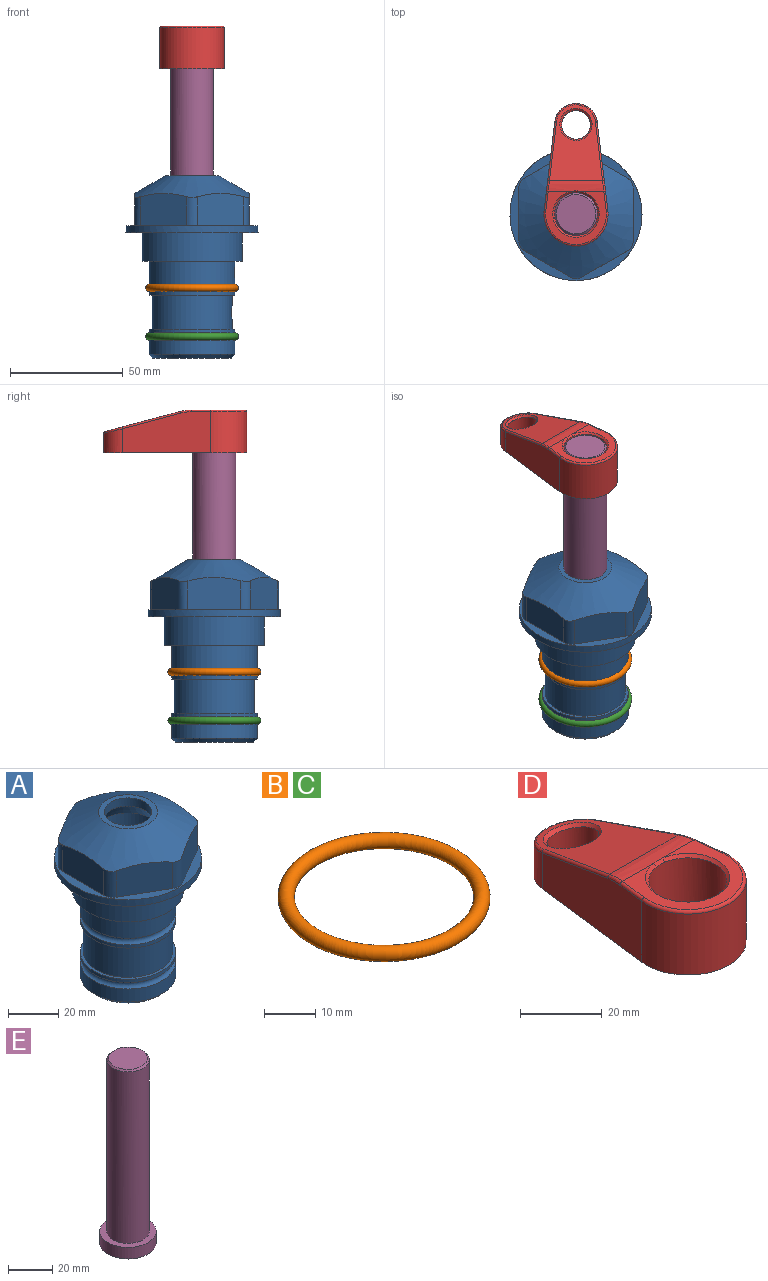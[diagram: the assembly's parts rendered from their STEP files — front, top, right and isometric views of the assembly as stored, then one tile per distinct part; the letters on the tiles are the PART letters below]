
ASSEMBLY  parts=5 mates=4
PART A: 36 faces, bbox 58.7x58.7x81 mm
  f0: cylinder r=17.78mm len=35.56mm, axis (0,0,1), area 1670.8mm2, adj f23,f24,f31
  f1: cylinder r=19.05mm len=38.1mm, axis (0,0,1), area 1191.9mm2, adj f26,f27,f30
  f2: plane 58.66x58.66mm, normal (0,0,-1), area 1150.6mm2, adj f3,f28
  f3: cylinder r=29.33mm len=58.66mm, axis (0,0,-1), area 585.1mm2, adj f2,f4
  f4: plane 58.66x58.66mm, normal (0,0,1), area 475.9mm2, adj f3,f5,f6,f7,f8,f9,f10,f11
  f5: plane 20.32x14.34mm, normal (-0.5,0.87,0), area 324.4mm2, adj f4,f15,f16,f17
  f6: plane 20.32x14.34mm, normal (0.5,0.87,0), area 324.4mm2, adj f4,f14,f15,f17
  f7: plane 23.48x14.34mm, normal (1,0,0), area 324.4mm2, adj f4,f13,f14,f17
  f8: plane 20.32x14.34mm, normal (0.5,-0.87,0), area 324.4mm2, adj f4,f12,f13,f17
  f9: plane 20.32x14.34mm, normal (-0.5,-0.87,0), area 324.4mm2, adj f4,f11,f12,f17
  f10: plane 23.48x14.34mm, normal (-1,0,0), area 324.4mm2, adj f4,f11,f16,f17
  f11: cylinder r=5.08mm len=12.85mm, axis (0,0,-1), area 67.2mm2, adj f4,f9,f10,f17
  f12: cylinder r=5.08mm len=12.85mm, axis (0,0,-1), area 67.2mm2, adj f4,f8,f9,f17
  f13: cylinder r=5.08mm len=12.85mm, axis (0,0,-1), area 67.2mm2, adj f4,f7,f8,f17
  f14: cylinder r=5.08mm len=12.85mm, axis (0,0,-1), area 67.2mm2, adj f4,f6,f7,f17
  f15: cylinder r=5.08mm len=12.85mm, axis (0,0,-1), area 67.2mm2, adj f4,f5,f6,f17
  f16: cylinder r=5.08mm len=12.85mm, axis (0,0,-1), area 67.2mm2, adj f4,f5,f10,f17
  f17: cone r=11.73mm half-angle=60deg, axis (0,0,-1), area 2071.8mm2, adj f5,f6,f7,f8,f9,f10,f11,f12
  f18: plane 23.46x23.46mm, normal (0,0,1), area 147.4mm2, adj f17,f35
  f19: plane 34.93x34.93mm, normal (0,0,-1), area 958mm2, adj f29
  f20: cylinder r=19.05mm len=38.1mm, axis (0,0,1), area 760.1mm2, adj f21,f29
  f21: torus R=19.05mm, axis (0,0,1), area 565.3mm2, adj f20,f22
  f22: cylinder r=19.05mm len=38.1mm, axis (0,0,1), area 190mm2, adj f21,f23
  f23: plane 38.1x38.1mm, normal (0,0,1), area 146.9mm2, adj f0,f22
  f24: plane 38.1x38.1mm, normal (0,0,-1), area 146.9mm2, adj f0,f25
  f25: cylinder r=19.05mm len=38.1mm, axis (0,0,1), area 190mm2, adj f24,f26
  f26: torus R=19.05mm, axis (0,0,1), area 565.3mm2, adj f1,f25
  f27: plane 44.45x44.45mm, normal (0,0,-1), area 411.7mm2, adj f1,f28
  f28: cylinder r=22.23mm len=44.45mm, axis (0,0,1), area 1773.5mm2, adj f2,f27
  f29: cone r=19.05mm half-angle=45deg, axis (0,0,1), area 257.5mm2, adj f19,f20
  f30: cylinder r=3.17mm len=6.75mm, axis (-1,0,0), area 128mm2, adj f1,f33
  f31: cylinder r=3.17mm len=6.35mm, axis (-1,0,0), area 102.5mm2, adj f0,f33
  f32: plane 25.4x25.4mm, normal (0,0,1), area 506.7mm2, adj f33
  f33: cylinder r=12.7mm len=66.42mm, axis (0,0,-1), area 5236.2mm2, adj f30,f31,f32,f34
  f34: cone r=9.53mm half-angle=30deg, axis (0,0,-1), area 443.4mm2, adj f33,f35
  f35: cylinder r=9.53mm len=19.05mm, axis (0,0,-1), area 240.9mm2, adj f18,f34
PART B: 1 faces, bbox 44.7x44.7x3.2 mm
  f0: torus R=19.05mm, axis (0,0,1), area 1193.9mm2
PART C: same geometry as B
PART D: 31 faces, bbox 31.7x65.5x19.8 mm
  f0: plane 39.12x18.26mm, normal (0.99,0.12,0), area 612.2mm2, adj f1,f4,f7,f11,f13,f15
  f1: cylinder r=9.53mm len=18.91mm, axis (0,0,-1), area 296.1mm2, adj f0,f2,f7,f17
  f2: plane 39.12x18.26mm, normal (-0.99,0.12,0), area 612.2mm2, adj f1,f4,f7,f12,f14,f16
  f3: cylinder r=6.35mm len=12.7mm, axis (0,0,-1), area 362.4mm2, adj f7,f18
  f4: cylinder r=14.29mm len=28.58mm, axis (0,0,-1), area 882.2mm2, adj f0,f2,f7,f10
  f5: cylinder r=9.53mm len=19.05mm, axis (0,0,-1), area 1092.6mm2, adj f7,f19,f20
  f6: plane 26.99x23.69mm, normal (0,0,1), area 216.2mm2, adj f9,f10,f11,f12,f19
  f7: plane 63.5x28.58mm, normal (0,0,-1), area 661.8mm2, adj f0,f1,f2,f3,f4,f5,f22,f23
  f8: plane 33.52x23.6mm, normal (0,0.26,0.97), area 486mm2, adj f9,f15,f16,f17,f18
  f9: cylinder r=19.05mm len=24.72mm, axis (1,0,0), area 120.4mm2, adj f6,f8,f13,f14,f20
  f10: torus R=13.49mm, axis (0,0,1), area 59mm2, adj f4,f6,f11,f12
  f11: cylinder r=0.79mm len=8.67mm, axis (0.12,-0.99,0), area 10.8mm2, adj f0,f6,f10,f13
  f12: cylinder r=0.79mm len=8.67mm, axis (0.12,0.99,0), area 10.8mm2, adj f2,f6,f10,f14
  f13: bspline ~4.95x1.42mm, area 6.1mm2, adj f0,f9,f11,f15
  f14: bspline ~4.95x1.42mm, area 6.1mm2, adj f2,f9,f12,f16
  f15: cylinder r=0.79mm len=25.95mm, axis (0.12,-0.96,0.26), area 32.9mm2, adj f0,f8,f13,f17
  f16: cylinder r=0.79mm len=25.95mm, axis (0.12,0.96,-0.26), area 32.9mm2, adj f2,f8,f14,f17
  f17: bspline ~18.91x8.38mm, area 30mm2, adj f1,f8,f15,f16
  f18: bspline ~14.29x14.29mm, area 48.3mm2, adj f3,f8
  f19: cone r=9.53mm half-angle=45deg, axis (0,0,1), area 66.5mm2, adj f5,f6,f20
  f20: bspline ~3.22x0.96mm, area 3.5mm2, adj f5,f9,f19
  f21: plane 2.75x2.72mm, normal (0,0,-1), area 2.9mm2, adj f23,f25,f28
  f22: plane 23.05x15.88mm, normal (-0.99,-0.12,0), area 323.6mm2, adj f7,f25,f26,f27,f28,f29
  f23: plane 23.05x15.88mm, normal (0.99,-0.12,0), area 323.6mm2, adj f7,f21,f25,f27,f28,f30
  f24: cylinder r=9.53mm len=10.69mm, axis (0,0,-1), area 114.7mm2, adj f7,f27,f29,f30
  f25: cylinder r=12.7mm len=20.59mm, axis (0,0,-1), area 381.1mm2, adj f7,f21,f22,f23,f26,f28
  f26: plane 2.75x2.72mm, normal (0,0,-1), area 2.9mm2, adj f22,f25,f28
  f27: plane 19.72x18.37mm, normal (0,-0.26,-0.97), area 291.8mm2, adj f22,f23,f24,f28,f29,f30
  f28: cylinder r=15.88mm len=19.92mm, axis (1,0,0), area 54.8mm2, adj f21,f22,f23,f25,f26,f27
  f29: cylinder r=1.59mm len=11mm, axis (0,0,-1), area 34.7mm2, adj f7,f22,f24,f27
  f30: cylinder r=1.59mm len=11mm, axis (0,0,-1), area 34.7mm2, adj f7,f23,f24,f27
PART E: 6 faces, bbox 25.4x25.4x101.6 mm
  f0: plane 17.46x17.46mm, normal (0,0,1), area 239.5mm2, adj f5
  f1: plane 25.4x25.4mm, normal (0,0,-1), area 506.7mm2, adj f2
  f2: cylinder r=12.7mm len=25.4mm, axis (0,0,1), area 506.7mm2, adj f1,f3
  f3: plane 25.4x25.4mm, normal (0,0,1), area 221.7mm2, adj f2,f4
  f4: cylinder r=9.53mm len=94.46mm, axis (0,0,1), area 5653mm2, adj f3,f5
  f5: cone r=8.73mm half-angle=45deg, axis (0,0,-1), area 64.4mm2, adj f0,f4
PLACE A at identity fixed
PLACE B at identity
PLACE C t=(0,0,-21.59)mm
PLACE D t=(0,0,28.35)mm
PLACE E t=(0,0,27.55)mm
MATE cylindrical A.f0 <-> E.f2  axis (0,0,1) through (0,0,-50.55)mm
MATE fastened B.f0 <-> A.f0  axis (0,0,1) through (0,0,-24.51)mm
MATE fastened D.f4 <-> E.f2  axis (0,0,-1) through (0,0,91.05)mm
MATE fastened C.f0 <-> A.f0  axis (0,0,1) through (0,0,-46.1)mm
